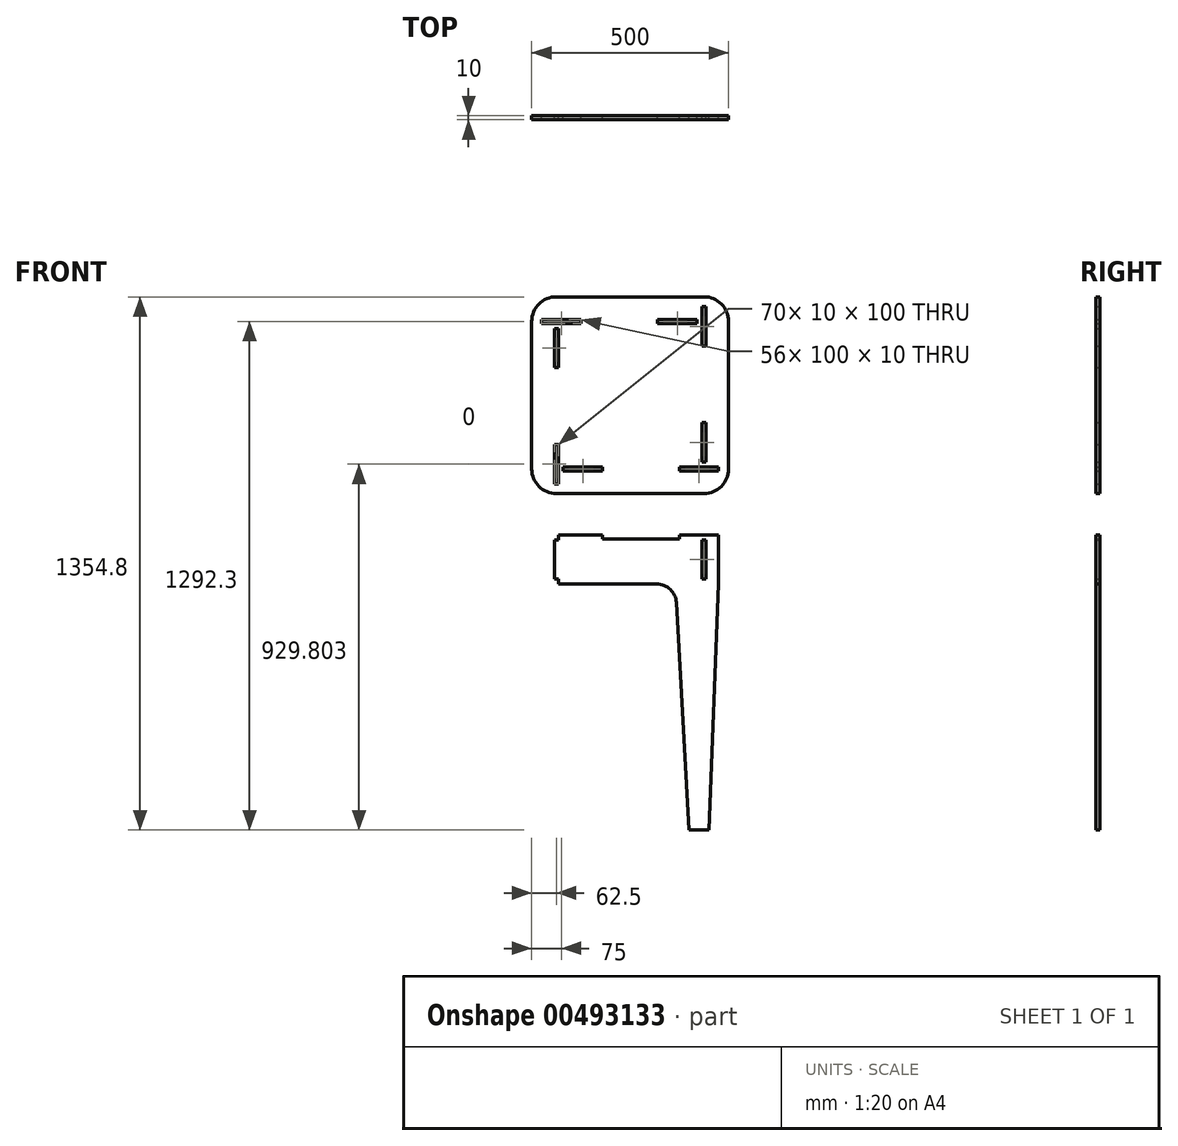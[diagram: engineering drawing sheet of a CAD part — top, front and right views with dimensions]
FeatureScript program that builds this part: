
annotation { "Feature Type Name" : "Feature", "Feature Type Description" : "" }
export const myFeature = defineFeature(function(context is Context, id is Id, definition is map)
    precondition{}
    {
        {
            var Q0;
            Q0=qCreatedBy(makeId("Front.planeOp"),FACE);
            var sketch = newSketch(context, id + "F0", { "sketchPlane" : qUnion([Q0])});
            skLineSegment(sketch, "E0", {"start": v(-187.5, 677.4) * mm, "end": v(187.5, 677.4) * mm});
            skLineSegment(sketch, "E1", {"start": v(250, 614.9) * mm, "end": v(250, 239.9) * mm});
            skLineSegment(sketch, "E2", {"start": v(187.5, 177.4) * mm, "end": v(-187.5, 177.4) * mm});
            skLineSegment(sketch, "E3", {"start": v(-250, 239.9) * mm, "end": v(-250, 614.9) * mm});
            skLineSegment(sketch, "E4", {"start": v(-225, 619.9) * mm, "end": v(-225, 609.9) * mm});
            skLineSegment(sketch, "E5", {"start": v(-225, 609.9) * mm, "end": v(-125, 609.9) * mm});
            skLineSegment(sketch, "E6", {"start": v(-125, 609.9) * mm, "end": v(-125, 619.9) * mm});
            skLineSegment(sketch, "E7", {"start": v(-125, 619.9) * mm, "end": v(-225, 619.9) * mm});
            skLineSegment(sketch, "E8", {"start": v(182.5, 552.4) * mm, "end": v(192.5, 552.4) * mm});
            skLineSegment(sketch, "E9", {"start": v(192.5, 552.4) * mm, "end": v(192.5, 652.4) * mm});
            skLineSegment(sketch, "E10", {"start": v(192.5, 652.4) * mm, "end": v(182.5, 652.4) * mm});
            skLineSegment(sketch, "E11", {"start": v(182.5, 652.4) * mm, "end": v(182.5, 552.4) * mm});
            skLineSegment(sketch, "E12", {"start": v(70, 619.9) * mm, "end": v(70, 609.9) * mm});
            skLineSegment(sketch, "E13", {"start": v(70, 609.9) * mm, "end": v(170, 609.9) * mm});
            skLineSegment(sketch, "E14", {"start": v(170, 609.9) * mm, "end": v(170, 619.9) * mm});
            skLineSegment(sketch, "E15", {"start": v(170, 619.9) * mm, "end": v(70, 619.9) * mm});
            skLineSegment(sketch, "E16", {"start": v(182.5, 257.4) * mm, "end": v(192.5, 257.4) * mm});
            skLineSegment(sketch, "E17", {"start": v(192.5, 257.4) * mm, "end": v(192.5, 357.4) * mm});
            skLineSegment(sketch, "E18", {"start": v(192.5, 357.4) * mm, "end": v(182.5, 357.4) * mm});
            skLineSegment(sketch, "E19", {"start": v(182.5, 357.4) * mm, "end": v(182.5, 257.4) * mm});
            skLineSegment(sketch, "E20", {"start": v(-182.5, 597.4) * mm, "end": v(-192.5, 597.4) * mm});
            skLineSegment(sketch, "E21", {"start": v(-192.5, 597.4) * mm, "end": v(-192.5, 497.4) * mm});
            skLineSegment(sketch, "E22", {"start": v(-192.5, 497.4) * mm, "end": v(-182.5, 497.4) * mm});
            skLineSegment(sketch, "E23", {"start": v(-182.5, 497.4) * mm, "end": v(-182.5, 597.4) * mm});
            skLineSegment(sketch, "E24", {"start": v(-182.5, 302.4) * mm, "end": v(-192.5, 302.4) * mm});
            skLineSegment(sketch, "E25", {"start": v(-192.5, 302.4) * mm, "end": v(-192.5, 202.4) * mm});
            skLineSegment(sketch, "E26", {"start": v(-182.5, 202.4) * mm, "end": v(-182.5, 302.4) * mm});
            skLineSegment(sketch, "E27", {"start": v(-192.5, 202.4) * mm, "end": v(-182.5, 202.4) * mm});
            skLineSegment(sketch, "E28", {"start": v(225, 234.9) * mm, "end": v(225, 244.9) * mm});
            skLineSegment(sketch, "E29", {"start": v(225, 244.9) * mm, "end": v(125, 244.9) * mm});
            skLineSegment(sketch, "E30", {"start": v(125, 244.9) * mm, "end": v(125, 234.9) * mm});
            skLineSegment(sketch, "E31", {"start": v(125, 234.9) * mm, "end": v(225, 234.9) * mm});
            skLineSegment(sketch, "E32", {"start": v(-70, 234.9) * mm, "end": v(-70, 244.9) * mm});
            skLineSegment(sketch, "E33", {"start": v(-70, 244.9) * mm, "end": v(-170, 244.9) * mm});
            skLineSegment(sketch, "E34", {"start": v(-170, 244.9) * mm, "end": v(-170, 234.9) * mm});
            skLineSegment(sketch, "E35", {"start": v(-170, 234.9) * mm, "end": v(-70, 234.9) * mm});
            skArc(sketch, "E36", {"start": v(-250, 239.9) * mm, "mid": v(-231.7, 195.7) * mm, "end": v(-187.5, 177.4) * mm});
            skArc(sketch, "E37", {"start": v(-187.5, 677.4) * mm, "mid": v(-231.7, 659.1) * mm, "end": v(-250, 614.9) * mm});
            skArc(sketch, "E38", {"start": v(250, 614.9) * mm, "mid": v(231.7, 659.1) * mm, "end": v(187.5, 677.4) * mm});
            skArc(sketch, "E39", {"start": v(187.5, 177.4) * mm, "mid": v(231.7, 195.7) * mm, "end": v(250, 239.9) * mm});
            skLineSegment(sketch, "E40", {"start": v(125, 62.6) * mm, "end": v(-70, 62.6) * mm});
            skLineSegment(sketch, "E41", {"start": v(-70, 72.6) * mm, "end": v(-182.5, 72.6) * mm});
            skLineSegment(sketch, "E42", {"start": v(225, 72.6) * mm, "end": v(125, 72.6) * mm});
            skLineSegment(sketch, "E43", {"start": v(125, 72.6) * mm, "end": v(125, 62.6) * mm});
            skLineSegment(sketch, "E44", {"start": v(-182.5, 72.6) * mm, "end": v(-182.5, 60.1) * mm});
            skLineSegment(sketch, "E45", {"start": v(225, 72.6) * mm, "end": v(225, -52.4) * mm});
            skLineSegment(sketch, "E46", {"start": v(67.5, -52.4) * mm, "end": v(-182.5, -52.4) * mm});
            skLineSegment(sketch, "E47", {"start": v(-70, 72.6) * mm, "end": v(-70, 62.6) * mm});
            skLineSegment(sketch, "E48", {"start": v(-192.5, -39.9) * mm, "end": v(-182.5, -39.9) * mm});
            skLineSegment(sketch, "E49", {"start": v(-182.5, 60.1) * mm, "end": v(-192.5, 60.1) * mm});
            skLineSegment(sketch, "E50", {"start": v(-192.5, 60.1) * mm, "end": v(-192.5, -39.9) * mm});
            skLineSegment(sketch, "E51", {"start": v(-182.5, -39.9) * mm, "end": v(-182.5, -52.4) * mm});
            skLineSegment(sketch, "E52", {"start": v(192.5, 60.1) * mm, "end": v(182.5, 60.1) * mm});
            skLineSegment(sketch, "E53", {"start": v(182.5, 60.1) * mm, "end": v(182.5, -39.9) * mm});
            skLineSegment(sketch, "E54", {"start": v(192.5, -39.9) * mm, "end": v(192.5, 60.1) * mm});
            skLineSegment(sketch, "E55", {"start": v(182.5, -39.9) * mm, "end": v(192.5, -39.9) * mm});
            skLineSegment(sketch, "E56", {"start": v(225, -52.4) * mm, "end": v(200, -677.4) * mm});
            skLineSegment(sketch, "E57", {"start": v(200, -677.4) * mm, "end": v(150, -677.4) * mm});
            skLineSegment(sketch, "E58", {"start": v(150, -677.4) * mm, "end": v(117.42, -99.59) * mm});
            skPoint(sketch, "E59.visualSharp", {"position": v(114.76, -52.4) * mm});
            skArc(sketch, "E59.filletArc", {"start": v(117.42, -99.59) * mm, "mid": v(101.85, -66.07) * mm, "end": v(67.5, -52.4) * mm});
            skLineSegment(sketch, "E60", {"start": v(-250, 427.4) * mm, "end": v(250, 427.4) * mm});
            skLineSegment(sketch, "E61", {"start": v(0, 677.4) * mm, "end": v(0, 177.4) * mm});
            skSolve(sketch);
        }
        {
            var Q0;
            Q0=qSketchRegion(id+"F0",true);
            extrude(context, id + "F1", {"entities" : qUnion([Q0]), "depth" : 10 * mm});
        }
    });
